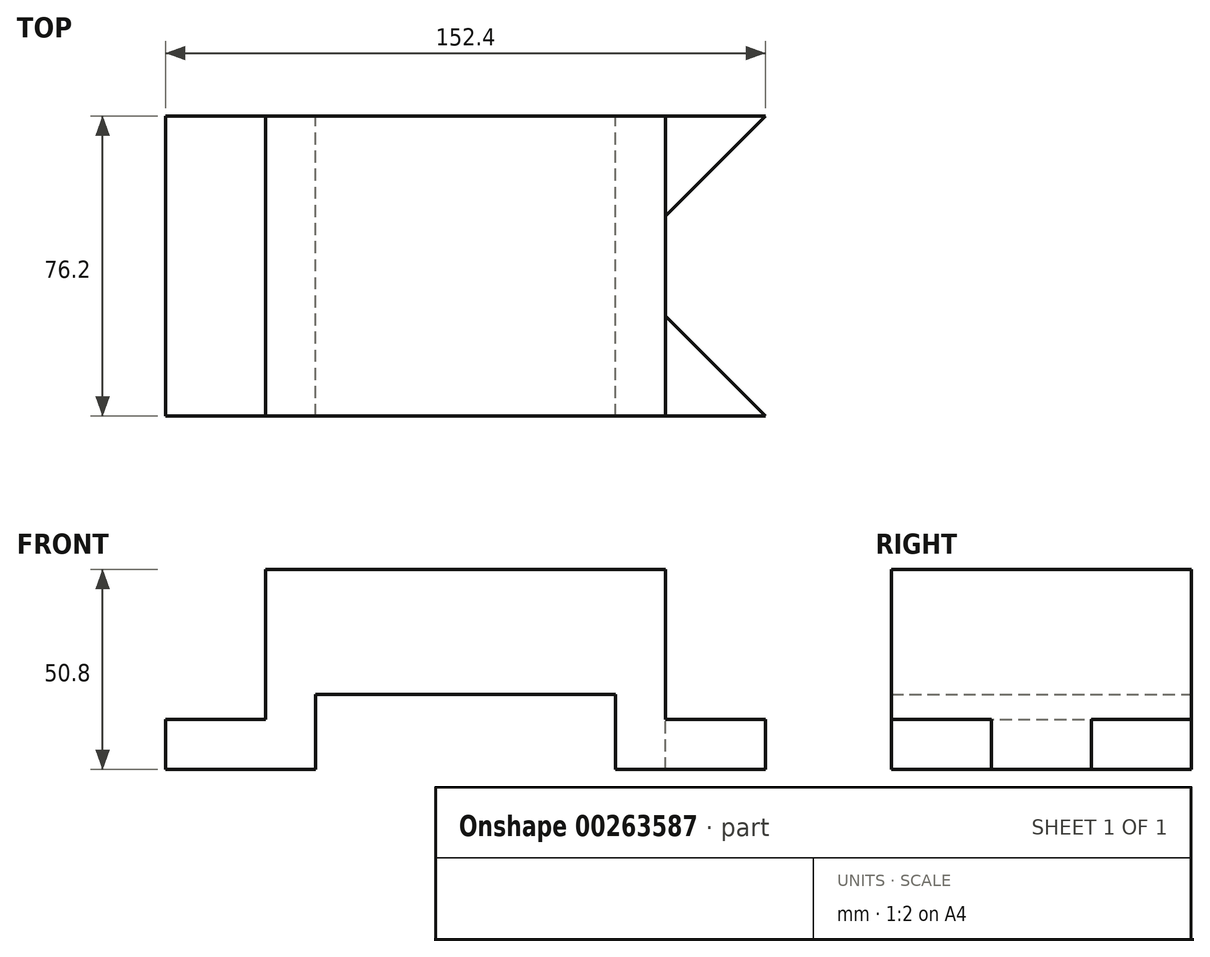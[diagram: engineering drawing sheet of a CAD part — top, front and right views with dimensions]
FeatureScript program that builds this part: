
annotation { "Feature Type Name" : "Feature", "Feature Type Description" : "" }
export const myFeature = defineFeature(function(context is Context, id is Id, definition is map)
    precondition{}
    {
        {
            var Q0;
            Q0=qCreatedBy(makeId("Front.planeOp"),FACE);
            var sketch = newSketch(context, id + "F0", { "sketchPlane" : qUnion([Q0])});
            skLineSegment(sketch, "E0.bottom", {"start": v(0, 0) * mm, "end": v(101.6, 0) * mm});
            skLineSegment(sketch, "E0.top", {"start": v(0, 50.8) * mm, "end": v(101.6, 50.8) * mm});
            skLineSegment(sketch, "E0.left", {"start": v(0, 12.7) * mm, "end": v(0, 50.8) * mm});
            skLineSegment(sketch, "E0.right", {"start": v(101.6, 0) * mm, "end": v(101.6, 50.8) * mm});
            skLineSegment(sketch, "E1", {"start": v(0, 0) * mm, "end": v(12.7, 0) * mm});
            skLineSegment(sketch, "E2", {"start": v(12.7, 0) * mm, "end": v(12.7, 19.05) * mm});
            skLineSegment(sketch, "E3", {"start": v(12.7, 19.05) * mm, "end": v(88.9, 19.05) * mm});
            skLineSegment(sketch, "E4", {"start": v(88.9, 19.05) * mm, "end": v(88.9, 0) * mm});
            skLineSegment(sketch, "E5", {"start": v(88.9, 0) * mm, "end": v(101.6, 0) * mm});
            skLineSegment(sketch, "E6", {"start": v(0, 0) * mm, "end": v(-25.4, 0) * mm});
            skLineSegment(sketch, "E7", {"start": v(-25.4, 0) * mm, "end": v(-25.4, 12.7) * mm});
            skLineSegment(sketch, "E8", {"start": v(-25.4, 12.7) * mm, "end": v(0, 12.7) * mm});
            skLineSegment(sketch, "E9", {"start": v(101.6, 0) * mm, "end": v(127, 0) * mm});
            skLineSegment(sketch, "E10", {"start": v(127, 0) * mm, "end": v(127, 12.7) * mm});
            skLineSegment(sketch, "E11", {"start": v(127, 12.7) * mm, "end": v(101.6, 12.7) * mm});
            skSolve(sketch);
        }
        {
            var Q0;
            Q0=makeQuery(id+"F0.imprint","IMPRINT",FACE,{"disambiguationData":[TD([[makeQuery(id+"F0.imprint","IMPRINT",EDGE,{"derivedFrom":sQuery(id+"F0.wireOp",EDGE,"E0.top")}),-1.0]])]});
            extrude(context, id + "F1", {"entities" : qUnion([Q0]), "depth" : 76.2 * mm});
        }
        {
            var Q0;
            {var subQ0=sQuery(id+"F0.wireOp",EDGE,"E9");Q0=makeQuery(id+"F0.imprint","IMPRINT",FACE,{"disambiguationData":[TD([[makeQuery(id+"F0.imprint","IMPRINT",EDGE,{"derivedFrom":subQ0}),1.0]])]});}
            extrude(context, id + "F2", {"entities" : qUnion([Q0]), "operationType" : NewBodyOperationType.ADD, "depth" : 76.2 * mm});
        }
        {
            var Q0;
            Q0=makeQuery(id+"F2.opExtrude","SWEPT_FACE",FACE,{"disambiguationData":[OSD([sQuery(id+"F0.wireOp",EDGE,"E11")])]});
            var sketch = newSketch(context, id + "F3", { "sketchPlane" : qUnion([Q0])});
            skLineSegment(sketch, "E12", {"start": v(101.6, -76.2) * mm, "end": v(101.6, -50.8) * mm});
            skLineSegment(sketch, "E13", {"start": v(101.6, -50.8) * mm, "end": v(127, -76.2) * mm});
            skLineSegment(sketch, "E14", {"start": v(127, -76.2) * mm, "end": v(101.6, -76.2) * mm});
            skLineSegment(sketch, "E15", {"start": v(101.6, 0) * mm, "end": v(101.6, -25.4) * mm});
            skLineSegment(sketch, "E16", {"start": v(101.6, -25.4) * mm, "end": v(127, 0) * mm});
            skLineSegment(sketch, "E17", {"start": v(127, 0) * mm, "end": v(101.6, 0) * mm});
            skSolve(sketch);
        }
        {
            var Q0;
            {var subQ0=sQuery(id+"F3.wireOp",EDGE,"E13");Q0=makeQuery(id+"F3.imprint","IMPRINT",FACE,{"disambiguationData":[TD([[makeQuery(id+"F3.imprint","IMPRINT",EDGE,{"derivedFrom":subQ0}),1.0]])]});}
            extrude(context, id + "F4", {"entities" : qUnion([Q0]), "operationType" : NewBodyOperationType.REMOVE, "oppositeDirection" : true, "depth" : 25.4 * mm});
        }
    });
